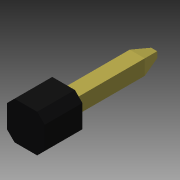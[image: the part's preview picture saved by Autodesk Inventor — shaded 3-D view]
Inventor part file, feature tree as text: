
AUTODESK INVENTOR PART (.ipt)
format: ipt  version: 2013 SP2 (Build 170200200, 200)  size: 108,544 bytes
history: native  units: mm
features: extrude x2, chamfer x2, sketch x2
ambient origin geometry x8: Origin, YZ Plane, XZ Plane, XY Plane, X Axis, Y Axis, Z Axis, Center Point
bodies: Solid1 (feature_tree)
feature tree (6):
  extrude  "Extrusion1"  Depth=2.5mm
  chamfer  "Chamfer1"  Distance=2.5mm
  extrude  "Extrusion2"  Depth=1.0mm
  chamfer  "Chamfer2"  Distance=1.0mm
  sketch  "Sketch1"  dims[d0=2.5mm d1=2.5mm d2=2.5mm d3=0.0mm]
  sketch  "Sketch2"  dims[d4=0.5mm d5=2.0mm d6=45.0deg d7=1.0mm d9=1.0mm d10=0.5mm d11=0.5mm d12=6.0mm d13=0.0mm d14=0.3mm d15=2.0mm d16=75.0deg]
